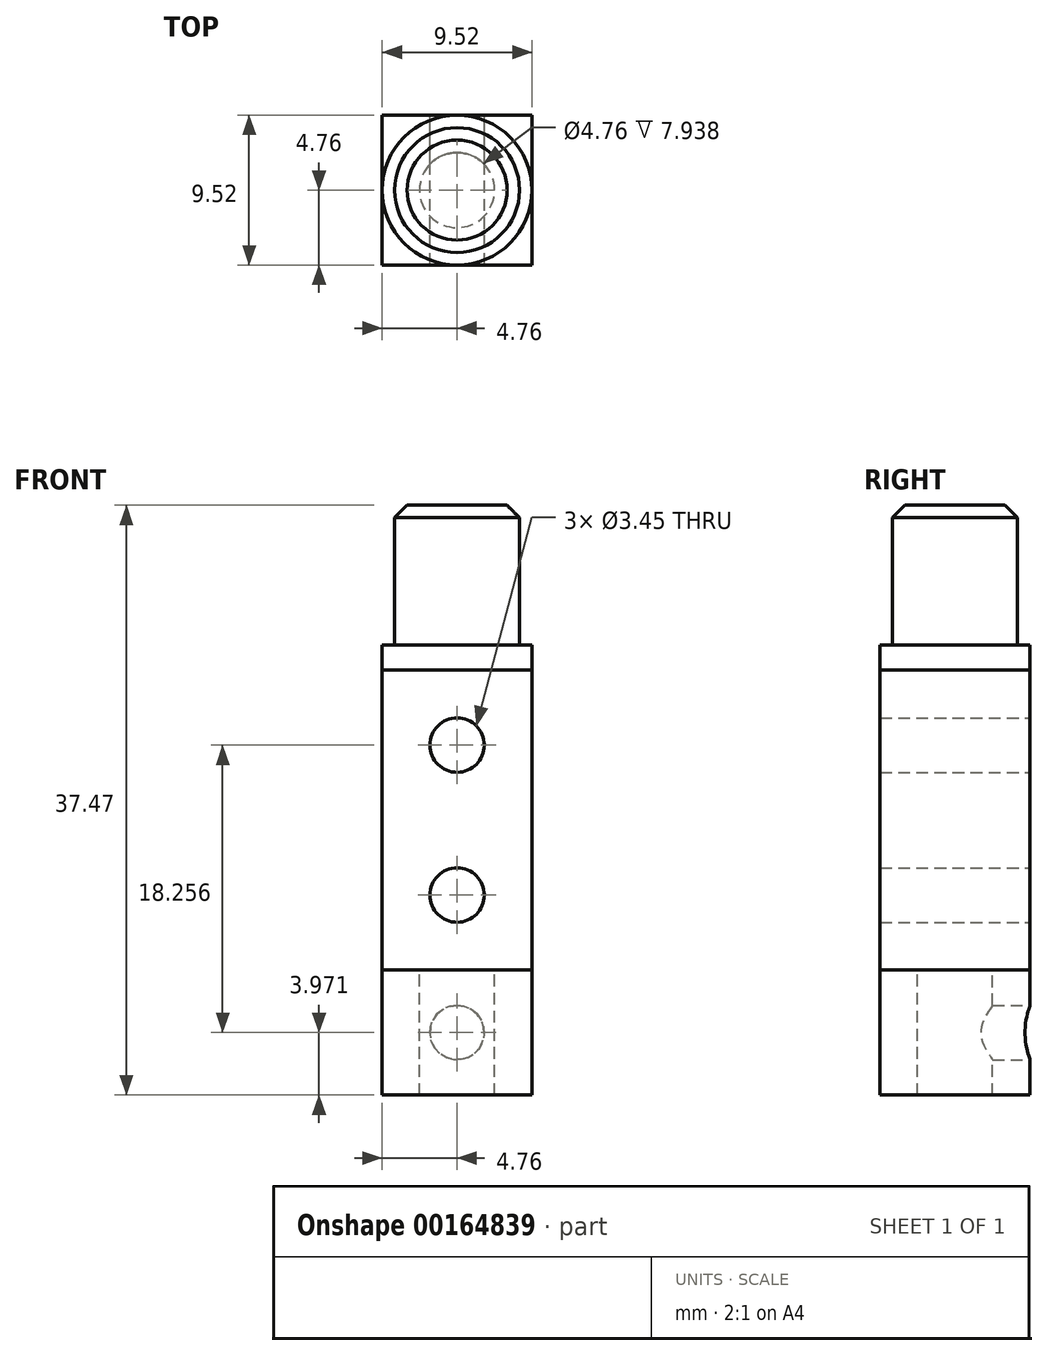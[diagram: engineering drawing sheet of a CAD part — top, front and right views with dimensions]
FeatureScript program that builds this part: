
annotation { "Feature Type Name" : "Feature", "Feature Type Description" : "" }
export const myFeature = defineFeature(function(context is Context, id is Id, definition is map)
    precondition{}
    {
        {
            var Q0;
            Q0=qCreatedBy(makeId("Top.planeOp"),FACE);
            var sketch = newSketch(context, id + "F0", { "sketchPlane" : qUnion([Q0])});
            skCircle(sketch, "E0", {"center": v(0, 0) * mm, "radius": 4.76 * mm});
            skSolve(sketch);
        }
        {
            var Q0;
            Q0=qSketchRegion(id+"F0",true);
            extrude(context, id + "F1", {"entities" : qUnion([Q0]), "depth" : 1.59 * mm});
        }
        {
            var Q0;
            Q0=makeQuery(id+"F1.opExtrude","CAP_FACE",FACE,{"disambiguationData":[OSD([sQuery(id+"F0.wireOp",EDGE,"E0")])],"isStart":false});
            var sketch = newSketch(context, id + "F2", { "sketchPlane" : qUnion([Q0])});
            skCircle(sketch, "E1", {"center": v(0, 0) * mm, "radius": 3.97 * mm});
            skSolve(sketch);
        }
        {
            var Q0;
            Q0=qSketchRegion(id+"F2",true);
            extrude(context, id + "F3", {"entities" : qUnion([Q0]), "operationType" : NewBodyOperationType.ADD, "depth" : 8.9 * mm});
        }
        {
            var Q0;
            Q0=makeQuery(id+"F1.opExtrude","CAP_FACE",FACE,{"disambiguationData":[OSD([sQuery(id+"F0.wireOp",EDGE,"E0")])],"isStart":true});
            var sketch = newSketch(context, id + "F4", { "sketchPlane" : qUnion([Q0])});
            skLineSegment(sketch, "E2.bottom", {"start": v(-4.76, -4.76) * mm, "end": v(4.76, -4.76) * mm});
            skLineSegment(sketch, "E2.top", {"start": v(-4.76, 4.76) * mm, "end": v(4.76, 4.76) * mm});
            skLineSegment(sketch, "E2.left", {"start": v(-4.76, -4.76) * mm, "end": v(-4.76, 4.76) * mm});
            skLineSegment(sketch, "E2.right", {"start": v(4.76, -4.76) * mm, "end": v(4.76, 4.76) * mm});
            skPoint(sketch, "E2.middle", {"position": v(0, 0) * mm});
            skSolve(sketch);
        }
        {
            var Q0;
            Q0=qSketchRegion(id+"F4",true);
            extrude(context, id + "F5", {"entities" : qUnion([Q0]), "operationType" : NewBodyOperationType.ADD, "depth" : 19.05 * mm});
        }
        {
            var Q0;
            Q0=makeQuery(id+"F3.opExtrude","CAP_EDGE",EDGE,{"disambiguationData":[OSD([sQuery(id+"F2.wireOp",EDGE,"E1")])],"isStart":false});
            chamfer(context, id + "F6", {"entities" : qUnion([Q0]), "width" : 0.8 * mm, "tangentPropagation" : true});
        }
        {
            var Q0;
            Q0=makeQuery(id+"F5.opExtrude","CAP_FACE",FACE,{"disambiguationData":[OSD([sQuery(id+"F4.wireOp",EDGE,"E2.bottom"),sQuery(id+"F4.wireOp",EDGE,"E2.top"),sQuery(id+"F4.wireOp",EDGE,"E2.left"),sQuery(id+"F4.wireOp",EDGE,"E2.right")])],"isStart":false});
            var sketch = newSketch(context, id + "F7", { "sketchPlane" : qUnion([Q0])});
            skCircle(sketch, "E3", {"center": v(0, 0) * mm, "radius": 4.76 * mm});
            skCircle(sketch, "E4", {"center": v(0, 0) * mm, "radius": 2.38 * mm});
            skSolve(sketch);
        }
        {
            var Q0;
            Q0 = qSketchRegion(id + "F7", true);
            extrude(context, id + "F8", {"entities" : qUnion([Q0]), "operationType" : NewBodyOperationType.ADD, "depth" : 7.94 * mm});
        }
        {
            var Q0;
            Q0=makeQuery(id+"F5.opExtrude","SWEPT_FACE",FACE,{"disambiguationData":[OSD([sQuery(id+"F4.wireOp",EDGE,"E2.bottom")])]});
            var sketch = newSketch(context, id + "F9", { "sketchPlane" : qUnion([Q0])});
            skLineSegment(sketch, "E5.bottom", {"start": v(0, 0) * mm, "end": v(-4.76, 0) * mm, "construction": true});
            skLineSegment(sketch, "E5.top", {"start": v(0, -4.76) * mm, "end": v(-4.76, -4.76) * mm, "construction": true});
            skLineSegment(sketch, "E5.left", {"start": v(0, 0) * mm, "end": v(0, -4.76) * mm, "construction": true});
            skLineSegment(sketch, "E5.right", {"start": v(-4.76, 0) * mm, "end": v(-4.76, -4.76) * mm, "construction": true});
            skLineSegment(sketch, "E6.bottom", {"start": v(0, -19.05) * mm, "end": v(4.76, -19.05) * mm, "construction": true});
            skLineSegment(sketch, "E6.top", {"start": v(0, -14.29) * mm, "end": v(4.76, -14.29) * mm, "construction": true});
            skLineSegment(sketch, "E6.left", {"start": v(0, -19.05) * mm, "end": v(0, -14.29) * mm, "construction": true});
            skLineSegment(sketch, "E6.right", {"start": v(4.76, -19.05) * mm, "end": v(4.76, -14.29) * mm, "construction": true});
            skCircle(sketch, "E7", {"center": v(0, -4.76) * mm, "radius": 1.73 * mm});
            skCircle(sketch, "E8", {"center": v(0, -14.29) * mm, "radius": 1.73 * mm});
            skSolve(sketch);
        }
        {
            var Q0;
            Q0=qSketchRegion(id+"F9",true);
            var Q1;
            Q1=makeQuery(id+"F5.opExtrude","SWEPT_FACE",FACE,{"disambiguationData":[OSD([sQuery(id+"F4.wireOp",EDGE,"E2.top")])]});
            extrude(context, id + "F10", {"entities" : qUnion([Q0]), "operationType" : NewBodyOperationType.REMOVE, "endBound" : BoundingType.UP_TO_SURFACE, "oppositeDirection" : true, "endBoundEntityFace" : qUnion([Q1]), "depth" : 25.4 * mm});
        }
        {
            var Q0;
            Q0=makeQuery(id+"F5.opExtrude","SWEPT_FACE",FACE,{"disambiguationData":[OSD([sQuery(id+"F4.wireOp",EDGE,"E2.bottom")])]});
            var sketch = newSketch(context, id + "F11", { "sketchPlane" : qUnion([Q0])});
            skLineSegment(sketch, "E9", {"start": v(0, -19.05) * mm, "end": v(0, -26.99) * mm, "construction": true});
            skCircle(sketch, "E10", {"center": v(0, -23.02) * mm, "radius": 1.73 * mm});
            skSolve(sketch);
        }
        {
            var Q0;
            Q0 = qSketchRegion(id + "F11", true);
            var Q1;
            Q1=makeQuery(id+"F8.opExtrude","SWEPT_FACE",FACE,{"disambiguationData":[OSD([sQuery(id+"F7.wireOp",EDGE,"E4")])]});
            extrude(context, id + "F12", {"entities" : qUnion([Q0]), "operationType" : NewBodyOperationType.REMOVE, "endBound" : BoundingType.UP_TO_SURFACE, "oppositeDirection" : true, "endBoundEntityFace" : qUnion([Q1]), "depth" : 25.4 * mm});
        }
    });
